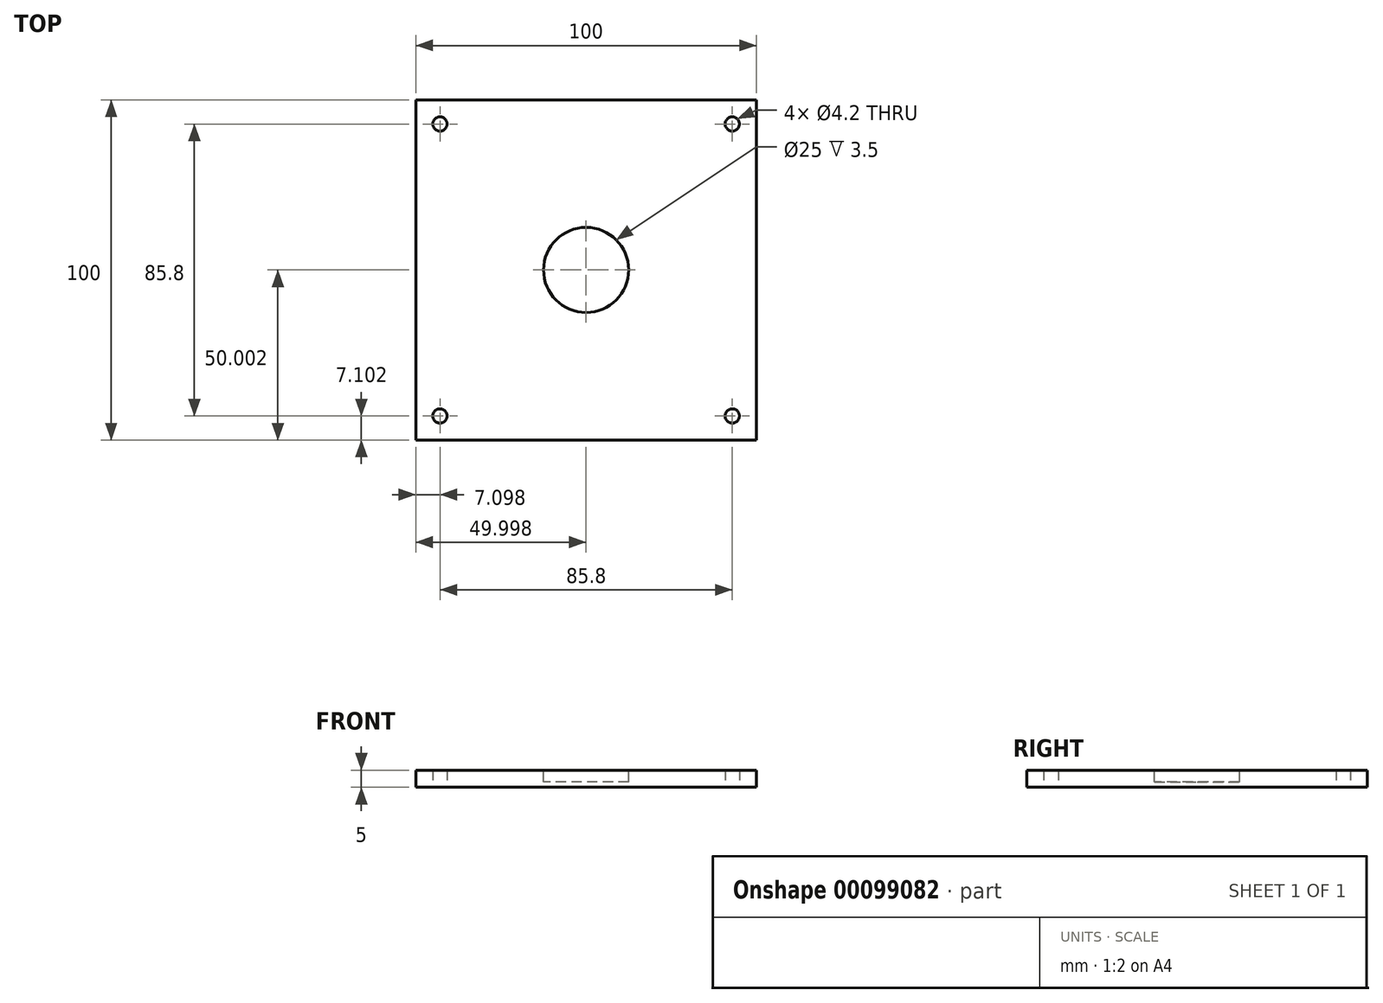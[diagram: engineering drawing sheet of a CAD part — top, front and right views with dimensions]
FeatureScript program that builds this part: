
annotation { "Feature Type Name" : "Feature", "Feature Type Description" : "" }
export const myFeature = defineFeature(function(context is Context, id is Id, definition is map)
    precondition{}
    {
        {
            var Q0;
            Q0=qCreatedBy(makeId("Top.planeOp"),FACE);
            var sketch = newSketch(context, id + "F0", { "sketchPlane" : qUnion([Q0])});
            skLineSegment(sketch, "E0.bottom", {"start": v(-41.88, 48.15) * mm, "end": v(58.12, 48.15) * mm});
            skLineSegment(sketch, "E0.top", {"start": v(-41.88, -51.85) * mm, "end": v(58.12, -51.85) * mm});
            skLineSegment(sketch, "E0.left", {"start": v(-41.88, 48.15) * mm, "end": v(-41.88, -51.85) * mm});
            skLineSegment(sketch, "E0.right", {"start": v(58.12, 48.15) * mm, "end": v(58.12, -51.85) * mm});
            skCircle(sketch, "E1", {"center": v(-34.78, 41.05) * mm, "radius": 2.1 * mm});
            skCircle(sketch, "E2", {"center": v(51.02, 41.05) * mm, "radius": 2.1 * mm});
            skCircle(sketch, "E3", {"center": v(51.02, -44.75) * mm, "radius": 2.1 * mm});
            skCircle(sketch, "E4", {"center": v(-34.78, -44.75) * mm, "radius": 2.1 * mm});
            skSolve(sketch);
        }
        {
            var Q0;
            Q0=makeQuery(id+"F0.imprint","IMPRINT",FACE,{"disambiguationData":[TD([[makeQuery(id+"F0.imprint","IMPRINT",EDGE,{"derivedFrom":sQuery(id+"F0.wireOp",EDGE,"E0.bottom")}),-1.0]])]});
            extrude(context, id + "F1", {"entities" : qUnion([Q0]), "depth" : 5 * mm});
        }
        {
            var Q0;
            Q0=makeQuery(id+"F1.opExtrude","CAP_FACE",FACE,{"disambiguationData":[OSD([sQuery(id+"F0.wireOp",EDGE,"E0.bottom"),sQuery(id+"F0.wireOp",EDGE,"E0.top"),sQuery(id+"F0.wireOp",EDGE,"E0.left"),sQuery(id+"F0.wireOp",EDGE,"E0.right"),sQuery(id+"F0.wireOp",EDGE,"E1"),sQuery(id+"F0.wireOp",EDGE,"E2"),sQuery(id+"F0.wireOp",EDGE,"E3"),sQuery(id+"F0.wireOp",EDGE,"E4")])],"isStart":false});
            var sketch = newSketch(context, id + "F2", { "sketchPlane" : qUnion([Q0])});
            skCircle(sketch, "E5", {"center": v(8.12, -1.85) * mm, "radius": 12.5 * mm});
            skSolve(sketch);
        }
        {
            var Q0;
            Q0 = qSketchRegion(id + "F2", true);
            extrude(context, id + "F3", {"entities" : qUnion([Q0]), "operationType" : NewBodyOperationType.REMOVE, "oppositeDirection" : true, "depth" : 3.5 * mm});
        }
    });
